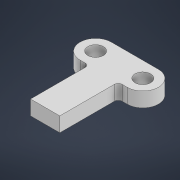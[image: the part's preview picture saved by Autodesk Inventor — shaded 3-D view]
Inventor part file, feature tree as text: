
AUTODESK INVENTOR PART (.ipt)
format: ipt  version: 2021 (Build 250183000, 183)  size: 127,488 bytes
history: native  units: mm
features: sketch x3, extrude x2, hole x1, fillet x1
ambient origin geometry x8: Origin, YZ Plane, XZ Plane, XY Plane, X Axis, Y Axis, Z Axis, Center Point
bodies: Solid1 (feature_tree)
feature tree (7):
  extrude  "Extrusion1"  Depth=8.0mm
  hole  "Hole1"  [1 undecoded]
  extrude  "Extrusion2"  TaperAngle=0.0deg  [1 undecoded]
  fillet  "Fillet1"  [1 undecoded]
  sketch  "Sketch1"  dims[d0=16.0mm d2=8.0mm]
  sketch  "Sketch2"  dims[d4=24.226mm d5=12.113mm]
  sketch  "Sketch3"  dims[d6=7.5mm d7=0.0mm d8=0.0mm d9=0.0mm d11=0.0mm d12=0.0mm d13=8.0mm d14=6.0mm d15=4.0mm d16=2.0mm d17=90.0deg d18=8.0mm d19=20.594885mm d20=15.0mm d21=7.5mm d22=30.0mm d23=0.0mm d24=2.0mm]
note: 3 required parameter values undecoded (feature->parameter linkage not recoverable at this tier; creation-order binding heuristic only, values carry confidence <= 0.55)
